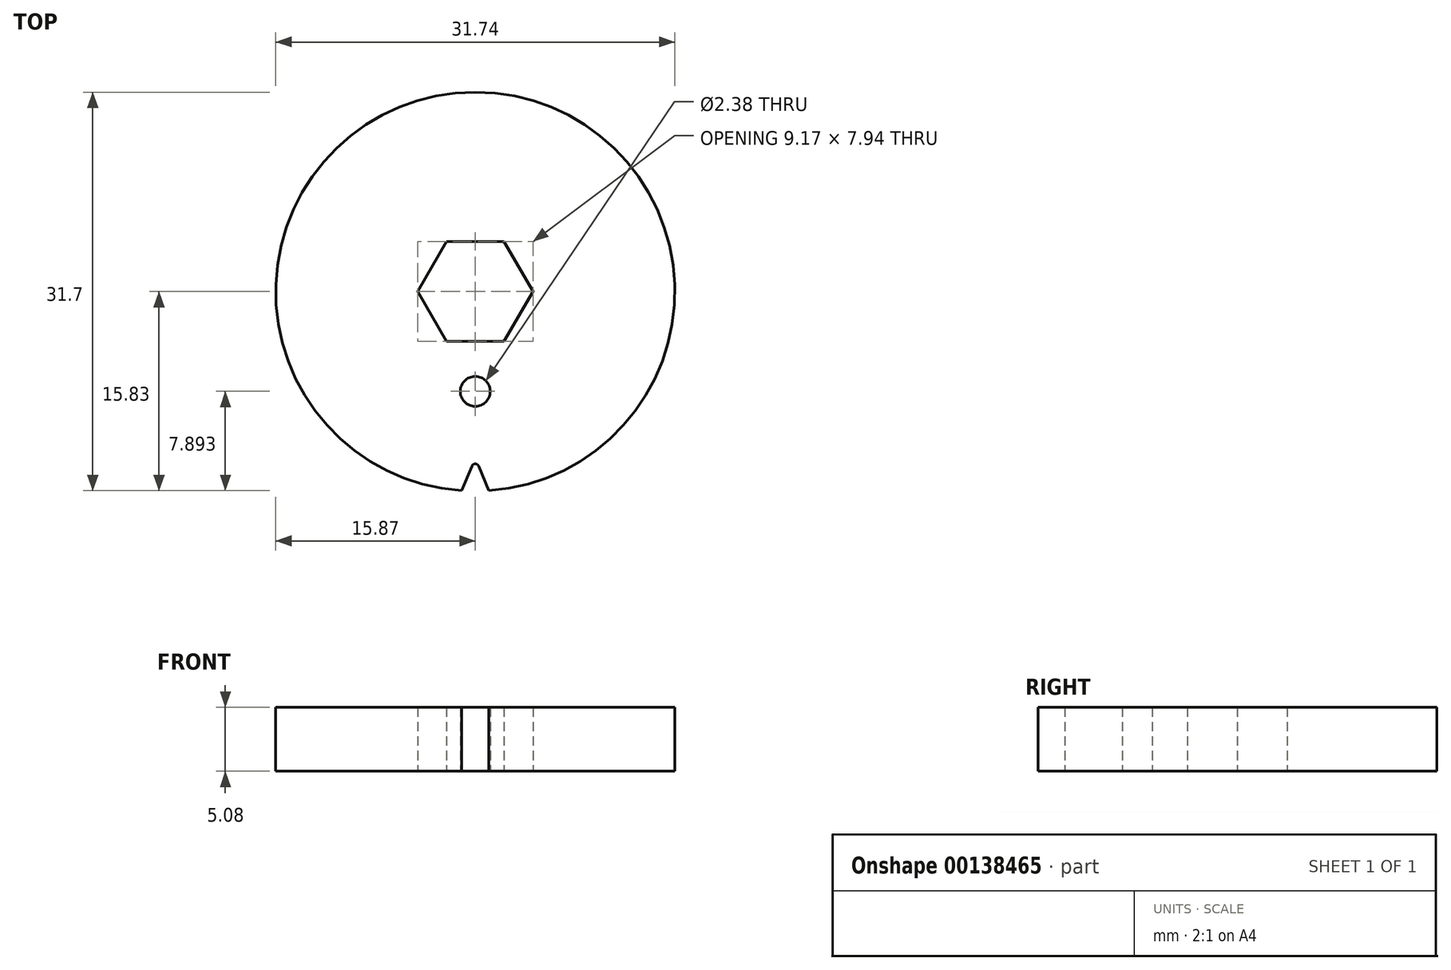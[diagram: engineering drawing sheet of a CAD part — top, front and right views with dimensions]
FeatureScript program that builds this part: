
annotation { "Feature Type Name" : "Feature", "Feature Type Description" : "" }
export const myFeature = defineFeature(function(context is Context, id is Id, definition is map)
    precondition{}
    {
        {
            var Q0;
            Q0=qCreatedBy(makeId("Top.planeOp"),FACE);
            var sketch = newSketch(context, id + "F0", { "sketchPlane" : qUnion([Q0])});
            skCircle(sketch, "E0", {"center": v(0, 0) * mm, "radius": 15.87 * mm});
            skCircle(sketch, "E1", {"center": v(0, 0) * mm, "radius": 5.56 * mm, "construction": true});
            skLineSegment(sketch, "E2", {"start": v(0, 0) * mm, "end": v(0, -7.94) * mm, "construction": true});
            skCircle(sketch, "E3", {"center": v(0, -7.94) * mm, "radius": 2.38 * mm, "construction": true});
            skCircle(sketch, "E4", {"center": v(0, -7.94) * mm, "radius": 1.2 * mm});
            skCircle(sketch, "E5.cCircle", {"center": v(0, 0) * mm, "radius": 3.97 * mm, "construction": true});
            skLineSegment(sketch, "E5.0", {"start": v(-2.3, 3.97) * mm, "end": v(2.3, 3.97) * mm});
            skLineSegment(sketch, "E5.1", {"start": v(2.3, 3.97) * mm, "end": v(4.58, 0) * mm});
            skLineSegment(sketch, "E5.2", {"start": v(4.58, 0) * mm, "end": v(2.3, -3.97) * mm});
            skLineSegment(sketch, "E5.3", {"start": v(2.3, -3.97) * mm, "end": v(-2.3, -3.97) * mm});
            skLineSegment(sketch, "E5.4", {"start": v(-2.3, -3.97) * mm, "end": v(-4.58, 0) * mm});
            skLineSegment(sketch, "E5.5", {"start": v(-4.58, 0) * mm, "end": v(-2.3, 3.97) * mm});
            skPoint(sketch, "E5.0.midPoint", {"position": v(0, 3.97) * mm});
            skSolve(sketch);
        }
        {
            var Q0;
            Q0=qSketchRegion(id+"F0",true);
            extrude(context, id + "F1", {"entities" : qUnion([Q0]), "depth" : 5.08 * mm});
        }
        {
            var Q0;
            Q0=makeQuery(id+"F1.opExtrude","CAP_FACE",FACE,{"disambiguationData":[OSD([sQuery(id+"F0.wireOp",EDGE,"1d9e0b5f-050f-40e5-a30c-8088f0055952.0"),sQuery(id+"F0.wireOp",EDGE,"1d9e0b5f-050f-40e5-a30c-8088f0055952.1"),sQuery(id+"F0.wireOp",EDGE,"1d9e0b5f-050f-40e5-a30c-8088f0055952.2"),sQuery(id+"F0.wireOp",EDGE,"1d9e0b5f-050f-40e5-a30c-8088f0055952.3"),sQuery(id+"F0.wireOp",EDGE,"1d9e0b5f-050f-40e5-a30c-8088f0055952.4"),sQuery(id+"F0.wireOp",EDGE,"1d9e0b5f-050f-40e5-a30c-8088f0055952.5"),sQuery(id+"F0.wireOp",EDGE,"1d9e0b5f-050f-40e5-a30c-8088f0055952.6"),sQuery(id+"F0.wireOp",EDGE,"1d9e0b5f-050f-40e5-a30c-8088f0055952.7"),sQuery(id+"F0.wireOp",EDGE,"E0"),sQuery(id+"F0.wireOp",EDGE,"cwqLcGPl-m7nu-ii5T-jM7M-63fMjzrrZEG8"),sQuery(id+"F0.wireOp",EDGE,"Ebe6PvGn-WY9l-eqVQ-QF1A-CMUX7UbrF9DL"),sQuery(id+"F0.wireOp",EDGE,"E44YlS9y-1Wgi-4iYU-zf0p-4PFYf8pnC5Qu"),sQuery(id+"F0.wireOp",EDGE,"w3ztLyFh-FlfK-Loua-tBJ6-JRWSCUkllsPx")])],"isStart":true});
            var sketch = newSketch(context, id + "F2", { "sketchPlane" : qUnion([Q0])});
            skLineSegment(sketch, "E6", {"start": v(0, 0) * mm, "end": v(0, 15.87) * mm, "construction": true});
            skLineSegment(sketch, "E7", {"start": v(0, 0) * mm, "end": v(0.73, 15.85) * mm, "construction": true});
            skArc(sketch, "E8", {"start": v(1.08, 15.83) * mm, "mid": v(0, 15.87) * mm, "end": v(-1.08, 15.83) * mm});
            skLineSegment(sketch, "E9", {"start": v(-1.08, 15.83) * mm, "end": v(-0.27, 13.89) * mm});
            skLineSegment(sketch, "E10", {"start": v(1.08, 15.83) * mm, "end": v(0.27, 13.89) * mm});
            skArc(sketch, "E11", {"start": v(-0.27, 13.89) * mm, "mid": v(0, 13.7) * mm, "end": v(0.27, 13.89) * mm});
            skPoint(sketch, "E12", {"position": v(0.68, 14.86) * mm});
            skSolve(sketch);
        }
        {
            var Q0;
            Q0=qSketchRegion(id+"F2",true);
            var Q1;
            Q1=makeQuery(id+"F1.opExtrude","CAP_FACE",FACE,{"disambiguationData":[OSD([sQuery(id+"F0.wireOp",EDGE,"1d9e0b5f-050f-40e5-a30c-8088f0055952.0"),sQuery(id+"F0.wireOp",EDGE,"1d9e0b5f-050f-40e5-a30c-8088f0055952.1"),sQuery(id+"F0.wireOp",EDGE,"1d9e0b5f-050f-40e5-a30c-8088f0055952.2"),sQuery(id+"F0.wireOp",EDGE,"1d9e0b5f-050f-40e5-a30c-8088f0055952.3"),sQuery(id+"F0.wireOp",EDGE,"1d9e0b5f-050f-40e5-a30c-8088f0055952.4"),sQuery(id+"F0.wireOp",EDGE,"1d9e0b5f-050f-40e5-a30c-8088f0055952.5"),sQuery(id+"F0.wireOp",EDGE,"1d9e0b5f-050f-40e5-a30c-8088f0055952.6"),sQuery(id+"F0.wireOp",EDGE,"1d9e0b5f-050f-40e5-a30c-8088f0055952.7"),sQuery(id+"F0.wireOp",EDGE,"E0"),sQuery(id+"F0.wireOp",EDGE,"cwqLcGPl-m7nu-ii5T-jM7M-63fMjzrrZEG8"),sQuery(id+"F0.wireOp",EDGE,"Ebe6PvGn-WY9l-eqVQ-QF1A-CMUX7UbrF9DL"),sQuery(id+"F0.wireOp",EDGE,"E44YlS9y-1Wgi-4iYU-zf0p-4PFYf8pnC5Qu"),sQuery(id+"F0.wireOp",EDGE,"w3ztLyFh-FlfK-Loua-tBJ6-JRWSCUkllsPx")])],"isStart":false});
            extrude(context, id + "F3", {"entities" : qUnion([Q0]), "operationType" : NewBodyOperationType.REMOVE, "endBound" : BoundingType.UP_TO_SURFACE, "oppositeDirection" : true, "endBoundEntityFace" : qUnion([Q1]), "depth" : 25.4 * mm});
        }
    });
